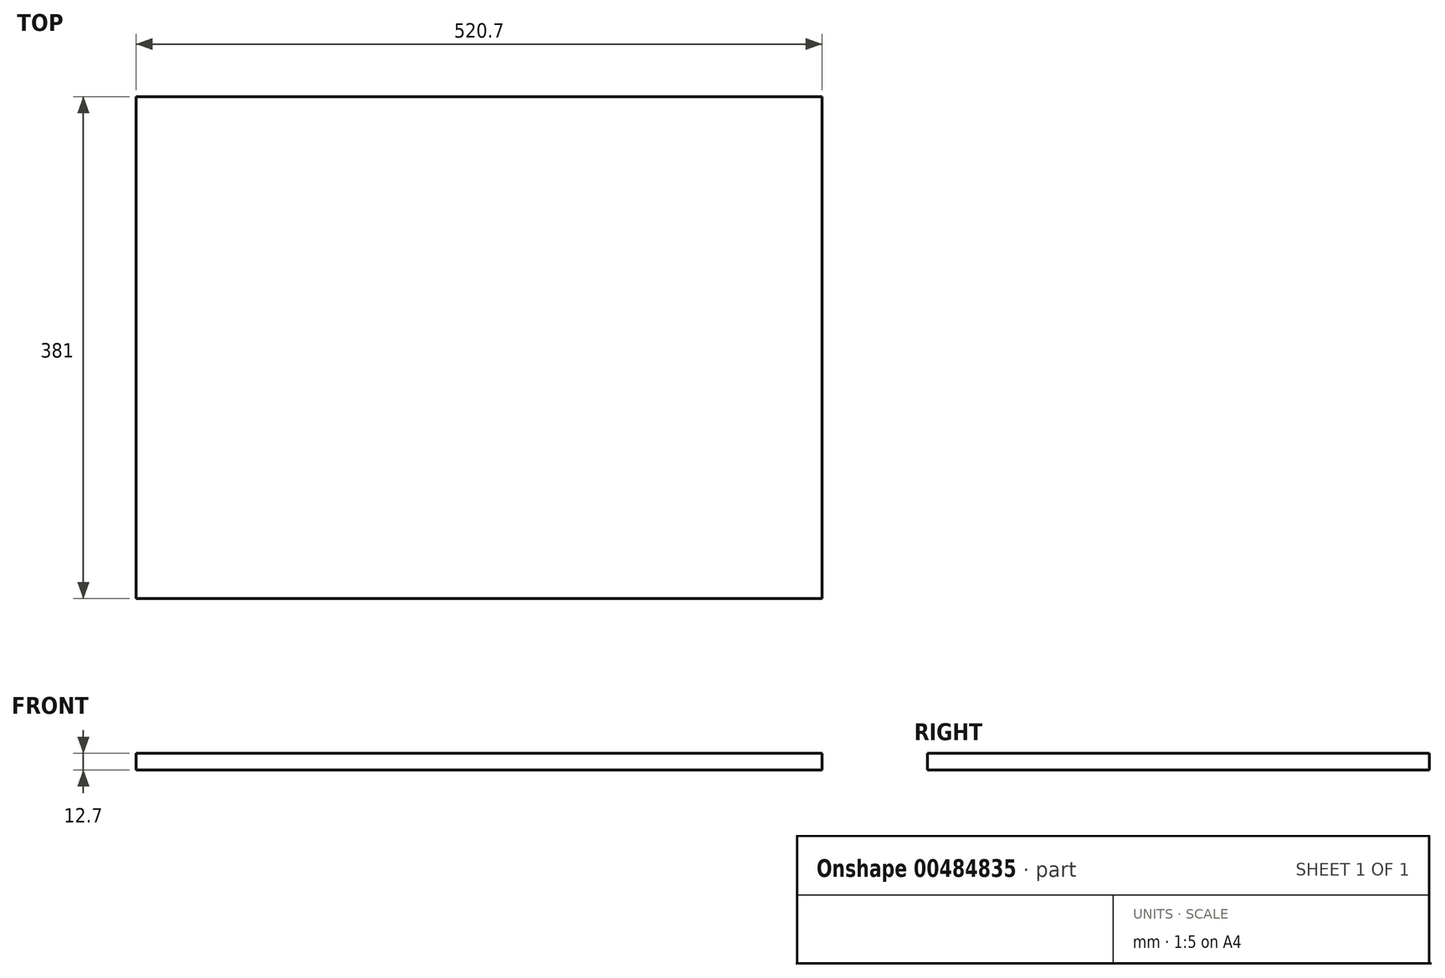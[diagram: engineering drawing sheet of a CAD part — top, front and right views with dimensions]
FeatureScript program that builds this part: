
annotation { "Feature Type Name" : "Feature", "Feature Type Description" : "" }
export const myFeature = defineFeature(function(context is Context, id is Id, definition is map)
    precondition{}
    {
        {
            var Q0;
            Q0=qCreatedBy(makeId("Top.planeOp"),FACE);
            var sketch = newSketch(context, id + "F0", { "sketchPlane" : qUnion([Q0])});
            skLineSegment(sketch, "E0.bottom", {"start": v(-260.35, 190.5) * mm, "end": v(260.35, 190.5) * mm});
            skLineSegment(sketch, "E0.top", {"start": v(-260.35, -190.5) * mm, "end": v(260.35, -190.5) * mm});
            skLineSegment(sketch, "E0.left", {"start": v(-260.35, 190.5) * mm, "end": v(-260.35, -190.5) * mm});
            skLineSegment(sketch, "E0.right", {"start": v(260.35, 190.5) * mm, "end": v(260.35, -190.5) * mm});
            skPoint(sketch, "E0.middle", {"position": v(0, 0) * mm});
            skSolve(sketch);
        }
        {
            var Q0;
            Q0 = qSketchRegion(id + "F0", true);
            extrude(context, id + "F1", {"entities" : qUnion([Q0]), "depth" : 12.7 * mm, "offsetDistance" : 25.4 * mm});
        }
    });
